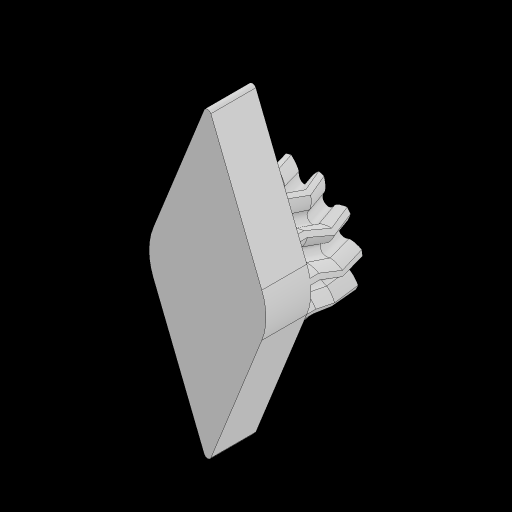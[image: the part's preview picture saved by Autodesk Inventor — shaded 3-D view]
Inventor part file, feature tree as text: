
AUTODESK INVENTOR PART (.ipt)
format: ipt  version: 2023.2 (Build 272271030, 271C)  size: 3,048,448 bytes
history: native  units: mm
features: sketch x4, extrude x4, projected_geometry x3, helix x1, pattern_circular x1, mirror x1, fillet x1
ambient origin geometry x8: Origin, YZ Plane, XZ Plane, XY Plane, X Axis, Y Axis, Z Axis, Center Point
bodies: Solid1 (feature_tree)
feature tree (15):
  sketch  "Sketch1"  dims[d0=2.5mm d1=0.0mm]
  extrude  "Extrusion1"  Depth=10.0mm TaperAngle=0.0deg
  helix  "Coil1"  [1 undecoded]
  pattern_circular  "Circular Pattern1"  [2 undecoded]
  mirror  "Mirror1"
  extrude  "Extrusion2"  [1 undecoded]
  extrude  "Extrusion3"  [1 undecoded]
  fillet  "Fillet1"  [1 undecoded]
  extrude  "Extrusion4"  [1 undecoded]
  sketch  "Sketch2"  dims[d2=110.1mm d3=10.0mm d4=10.0mm d5=0.0mm d6=90.0deg d7=90.0deg d8=0.0mm d9=0.0mm d10=110.0mm d11=360.0deg d13=1.0mm d14=0.0mm d15=35.0mm]
  projected_geometry  "Projected Loop1"
  sketch  "Sketch3"  dims[d16=5.0mm d17=0.0mm]
  projected_geometry  "Projected Loop2"
  sketch  "Sketch4"  dims[d18=0.4mm d19=0.25mm d20=0.0mm]
  projected_geometry  "Projected Loop3"
note: 7 required parameter values undecoded (feature->parameter linkage not recoverable at this tier; creation-order binding heuristic only, values carry confidence <= 0.55)
